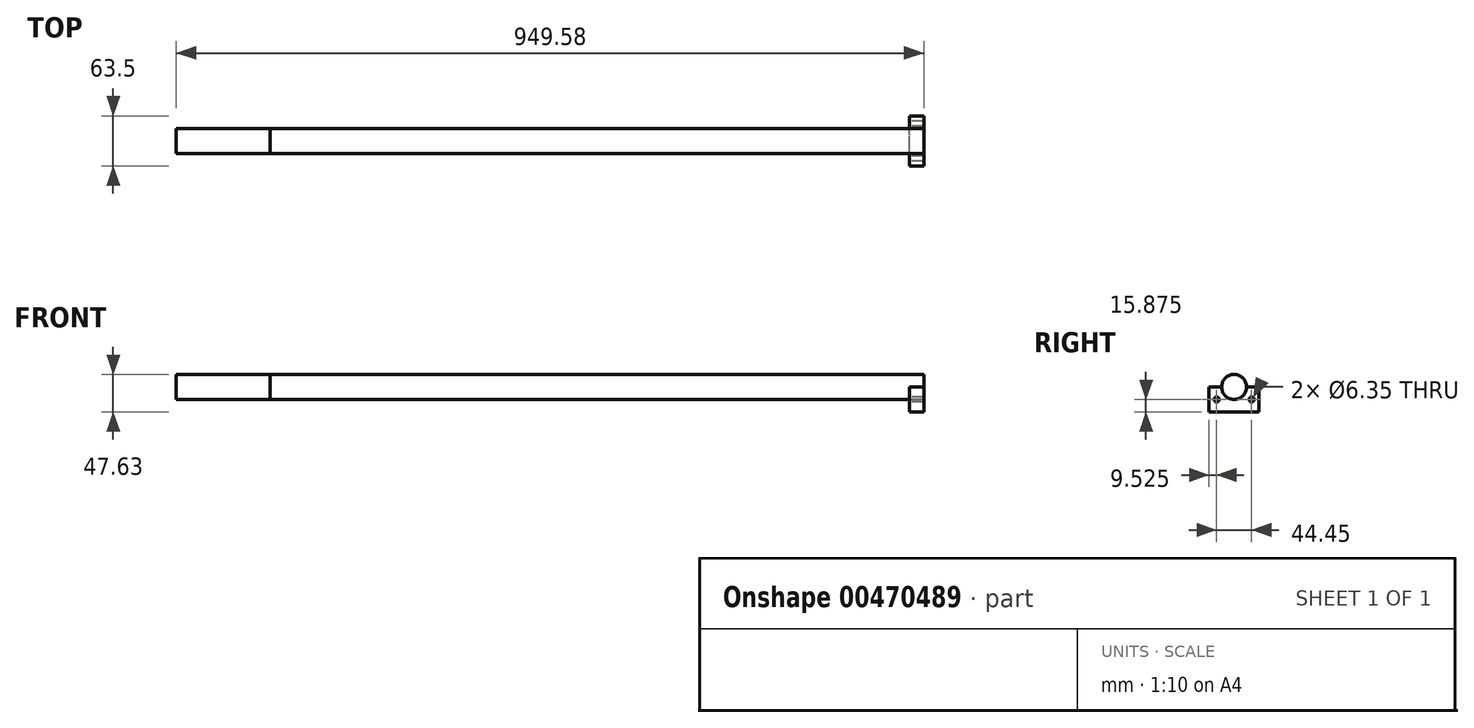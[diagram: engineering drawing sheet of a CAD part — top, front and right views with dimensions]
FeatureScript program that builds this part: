
annotation { "Feature Type Name" : "Feature", "Feature Type Description" : "" }
export const myFeature = defineFeature(function(context is Context, id is Id, definition is map)
    precondition{}
    {
        {
            var Q0;
            Q0=qCreatedBy(makeId("Right.planeOp"),FACE);
            var sketch = newSketch(context, id + "F0", { "sketchPlane" : qUnion([Q0])});
            skLineSegment(sketch, "E0.bottom", {"start": v(0, 0) * mm, "end": v(15.88, 0) * mm});
            skLineSegment(sketch, "E0.top", {"start": v(0, -31.75) * mm, "end": v(63.5, -31.75) * mm});
            skLineSegment(sketch, "E0.left", {"start": v(0, 0) * mm, "end": v(0, -31.75) * mm});
            skLineSegment(sketch, "E0.right", {"start": v(63.5, 0) * mm, "end": v(63.5, -31.75) * mm});
            skArc(sketch, "E1", {"start": v(15.88, 0) * mm, "mid": v(31.75, -15.88) * mm, "end": v(47.62, 0) * mm});
            skLineSegment(sketch, "E2.trimOffspring", {"start": v(47.62, 0) * mm, "end": v(63.5, 0) * mm});
            skCircle(sketch, "E3", {"center": v(9.52, -15.88) * mm, "radius": 3.18 * mm});
            skCircle(sketch, "E4", {"center": v(53.98, -15.87) * mm, "radius": 3.18 * mm});
            skSolve(sketch);
        }
        {
            var Q0;
            Q0=makeQuery(id+"F0.imprint","IMPRINT",FACE,{"disambiguationData":[TD([[makeQuery(id+"F0.imprint","IMPRINT",EDGE,{"derivedFrom":sQuery(id+"F0.wireOp",EDGE,"E0.bottom")}),-1.0]])]});
            extrude(context, id + "F1", {"entities" : qUnion([Q0]), "depth" : 18.29 * mm, "offsetDistance" : 25.4 * mm, "symmetric" : true});
        }
        {
            var Q0;
            Q0=makeQuery(id+"F1.opExtrude","CAP_FACE",FACE,{"disambiguationData":[OSD([sQuery(id+"F0.wireOp",EDGE,"E0.bottom"),sQuery(id+"F0.wireOp",EDGE,"E0.top"),sQuery(id+"F0.wireOp",EDGE,"E0.left"),sQuery(id+"F0.wireOp",EDGE,"E0.right"),sQuery(id+"F0.wireOp",EDGE,"E1"),sQuery(id+"F0.wireOp",EDGE,"E2.trimOffspring")])],"isStart":false});
            var sketch = newSketch(context, id + "F2", { "sketchPlane" : qUnion([Q0])});
            skCircle(sketch, "E5", {"center": v(31.75, 0) * mm, "radius": 15.88 * mm});
            skSolve(sketch);
        }
        {
            var Q0;
            {var subQ0=sQuery(id+"F2.wireOp",EDGE,"E5");var subQ1=makeQuery(id+"F2.imprint","INTERSECT",VERTEX,{"derivedFrom":[makeQuery(id+"F1.opExtrude","CAP_EDGE",EDGE,{"disambiguationData":[OSD([sQuery(id+"F0.wireOp",EDGE,"E0.bottom")])],"isStart":false}),subQ0]});Q0=makeQuery(id+"F2.imprint","IMPRINT",FACE,{"disambiguationData":[TD([[makeQuery(id+"F2.imprint","IMPRINT",EDGE,{"disambiguationData":[TD([[subQ1,1.0]])],"derivedFrom":subQ0}),1.0]])]});}
            extrude(context, id + "F3", {"entities" : qUnion([Q0]), "oppositeDirection" : true, "depth" : 830.26 * mm, "offsetDistance" : 25.4 * mm});
        }
        {
            var Q0;
            Q0=makeQuery(id+"F1.opExtrude","CAP_FACE",FACE,{"disambiguationData":[OSD([sQuery(id+"F0.wireOp",EDGE,"E0.bottom"),sQuery(id+"F0.wireOp",EDGE,"E0.top"),sQuery(id+"F0.wireOp",EDGE,"E0.left"),sQuery(id+"F0.wireOp",EDGE,"E0.right"),sQuery(id+"F0.wireOp",EDGE,"E1"),sQuery(id+"F0.wireOp",EDGE,"E2.trimOffspring")])],"isStart":false});
            var sketch = newSketch(context, id + "F4", { "sketchPlane" : qUnion([Q0])});
            skCircle(sketch, "E6", {"center": v(31.75, 0) * mm, "radius": 15.88 * mm});
            skSolve(sketch);
        }
        {
            var Q0;
            {var subQ0=sQuery(id+"F4.wireOp",EDGE,"E6");var subQ1=makeQuery(id+"F4.imprint","INTERSECT",VERTEX,{"derivedFrom":[makeQuery(id+"F1.opExtrude","CAP_EDGE",EDGE,{"disambiguationData":[OSD([sQuery(id+"F0.wireOp",EDGE,"E0.bottom")])],"isStart":false}),subQ0]});Q0=makeQuery(id+"F4.imprint","IMPRINT",FACE,{"disambiguationData":[TD([[makeQuery(id+"F4.imprint","IMPRINT",EDGE,{"disambiguationData":[TD([[subQ1,1.0]])],"derivedFrom":subQ0}),1.0]])]});}
            extrude(context, id + "F5", {"entities" : qUnion([Q0]), "oppositeDirection" : true, "depth" : 949.58 * mm, "offsetDistance" : 25.4 * mm});
        }
    });
